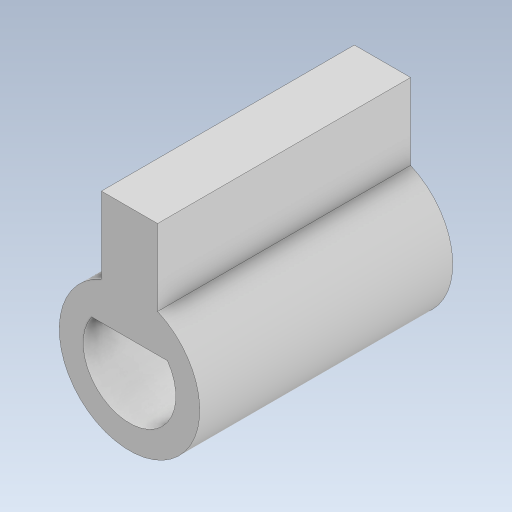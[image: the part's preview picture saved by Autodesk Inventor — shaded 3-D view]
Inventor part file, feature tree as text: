
AUTODESK INVENTOR PART (.ipt)
format: ipt  version: 2023.5 (Build 275446000, 446)  size: 286,720 bytes
history: native  units: in
note: dims shown in document units (in); Inventor stores cm internally (conversion verified against a paired STEP export)
features: extrude x1, sketch x1
ambient origin geometry x8: Origin, YZ Plane, XZ Plane, XY Plane, X Axis, Y Axis, Z Axis, Center Point
bodies: Solid1 (feature_tree)
feature tree (2):
  extrude  "Extrusion1"  Depth=0.0787in
  sketch  "Sketch1"  dims[d5=0.3543in d6=0.0in d16=0.1299in d18=0.0394in d29=0.1969in d30=0.0787in d31=0.1969in d8=0.0197in d9=0.0344in d10=0.0197in d11=0.0344in d20=0.0197in d21=0.0344in d22=0.0197in d23=0.0344in]
